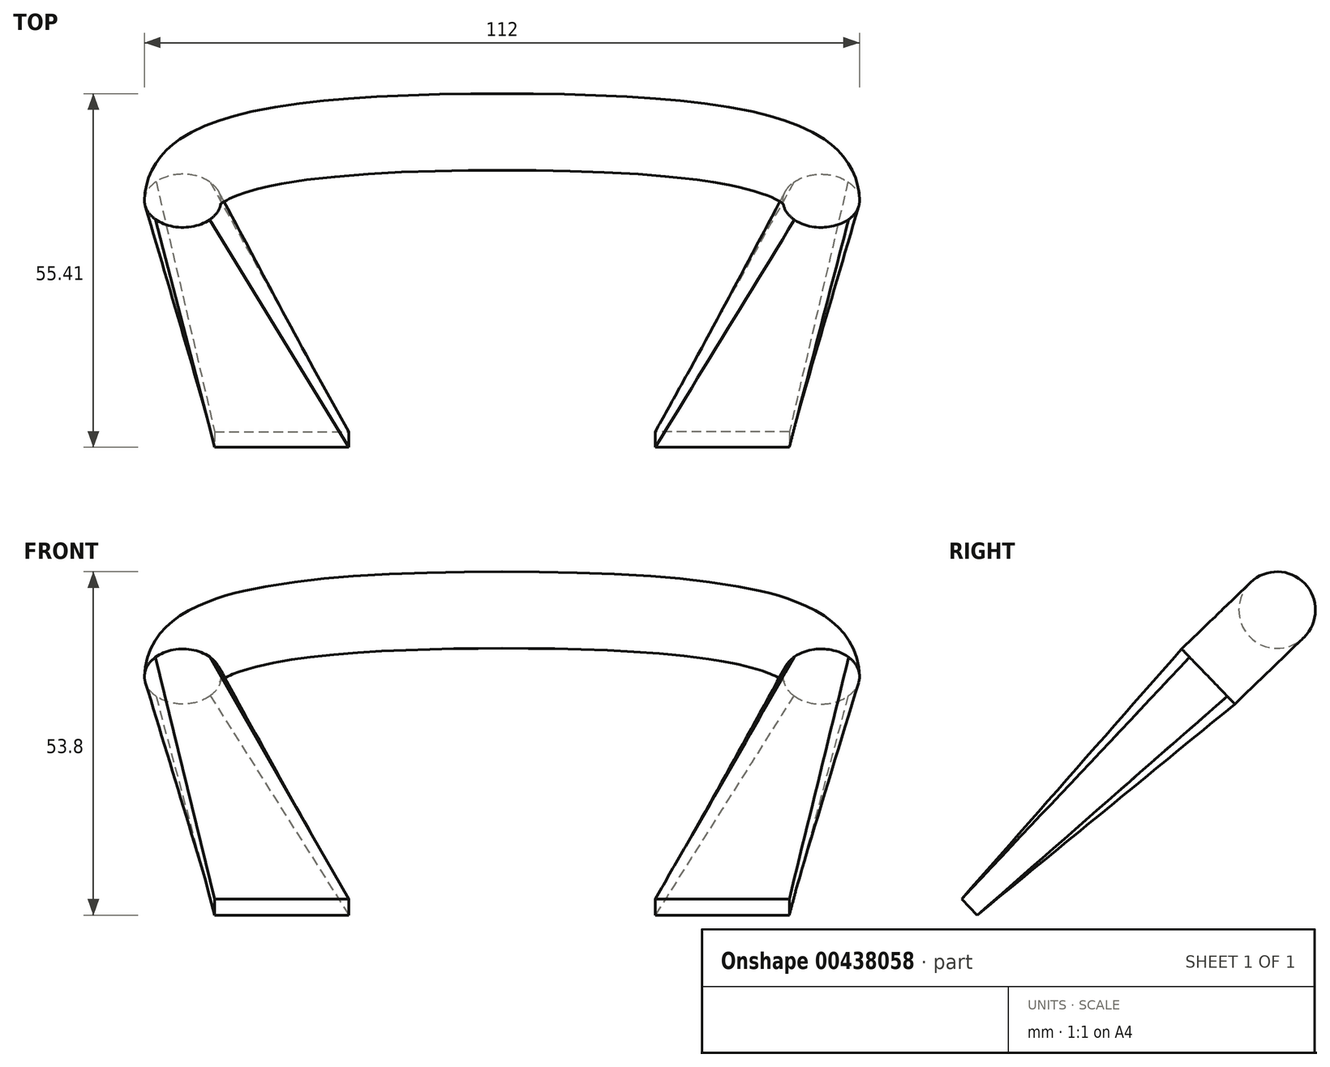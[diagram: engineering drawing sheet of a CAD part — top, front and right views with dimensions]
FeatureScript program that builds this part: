
annotation { "Feature Type Name" : "Feature", "Feature Type Description" : "" }
export const myFeature = defineFeature(function(context is Context, id is Id, definition is map)
    precondition{}
    {
        {
            var Q0;
            Q0=qCreatedBy(makeId("Top.planeOp"),FACE);
            var sketch = newSketch(context, id + "F0", { "sketchPlane" : qUnion([Q0])});
            skLineSegment(sketch, "E0", {"start": v(-34.5, 0) * mm, "end": v(34.5, 0) * mm, "construction": true});
            skLineSegment(sketch, "E1", {"start": v(0, 0) * mm, "end": v(0, 77.28) * mm, "construction": true});
            skPoint(sketch, "E2", {"position": v(-50, 52) * mm});
            skPoint(sketch, "E3", {"position": v(0, 67) * mm});
            skFitSpline(sketch, "E4", {"points": [v(0, 67) * mm, v(-50, 52) * mm], "startDerivative": vector(-102.6, 0) * mm, "endDerivative": vector(0, -30.42) * mm});
            skSolve(sketch);
        }
        {
            var Q0;
            Q0=qCreatedBy(makeId("Right.planeOp"),FACE);
            var sketch = newSketch(context, id + "F1", { "sketchPlane" : qUnion([Q0])});
            skPoint(sketch, "E5.0", {"position": v(67, 0) * mm});
            skCircle(sketch, "E6", {"center": v(67, 0) * mm, "radius": 6 * mm});
            skSolve(sketch);
        }
        {
            var Q0;
            Q0=makeQuery(id+"F1.imprint","IMPRINT",FACE,{"disambiguationData":[TD([[makeQuery(id+"F1.imprint","IMPRINT",EDGE,{"derivedFrom":sQuery(id+"F1.wireOp",EDGE,"E6")}),1.0]])]});
            var Q1;
            Q1=sQuery(id+"F0.wireOp",EDGE,"E4");
            sweep(context, id + "F2", {"profiles" : qUnion([Q0]), "path" : qUnion([Q1])});
        }
        {
            var Q0;
            Q0=qCreatedBy(makeId("Front.planeOp"),FACE);
            var sketch = newSketch(context, id + "F3", { "sketchPlane" : qUnion([Q0])});
            skLineSegment(sketch, "E7.0", {"start": v(-34.5, 0) * mm, "end": v(34.5, 0) * mm, "construction": true});
            skLineSegment(sketch, "E8.bottom", {"start": v(-45, -1.75) * mm, "end": v(-24, -1.75) * mm});
            skLineSegment(sketch, "E8.top", {"start": v(-45, 1.75) * mm, "end": v(-24, 1.75) * mm});
            skLineSegment(sketch, "E8.left", {"start": v(-45, -1.75) * mm, "end": v(-45, 1.75) * mm});
            skLineSegment(sketch, "E8.right", {"start": v(-24, -1.75) * mm, "end": v(-24, 1.75) * mm});
            skPoint(sketch, "E8.middle", {"position": v(-34.5, 0) * mm});
            skSolve(sketch);
        }
        {
            var Q0;
            Q0=makeQuery(id+"F2.opSweep","CAP_FACE",FACE,{"disambiguationData":[OSD([sQuery(id+"F0.wireOp",VERTEX,"E4.end"),sQuery(id+"F1.wireOp",EDGE,"E6")])],"isStart":false});
            var sketch = newSketch(context, id + "F4", { "sketchPlane" : qUnion([Q0])});
            skPoint(sketch, "E9.0", {"position": v(-50, 0) * mm});
            skPoint(sketch, "E10", {"position": v(-54.3, 4.19) * mm});
            skPoint(sketch, "E11", {"position": v(-45.7, 4.19) * mm});
            skPoint(sketch, "E12", {"position": v(-45.7, -4.19) * mm});
            skPoint(sketch, "E13", {"position": v(-54.3, -4.19) * mm});
            skSolve(sketch);
        }
        {
            var Q1;
            Q1=makeQuery(id+"F2.opSweep","CAP_FACE",FACE,{"disambiguationData":[OSD([sQuery(id+"F0.wireOp",VERTEX,"E4.end"),sQuery(id+"F1.wireOp",EDGE,"E6")])],"isStart":false});
            var Q2;
            Q2=makeQuery(id+"F3.imprint","IMPRINT",FACE,{"disambiguationData":[TD([[makeQuery(id+"F3.imprint","IMPRINT",EDGE,{"derivedFrom":sQuery(id+"F3.wireOp",EDGE,"E8.bottom")}),1.0]])]});
            var Q3;
            Q3=sQuery(id+"F3.wireOp",VERTEX,"E8.left.end");
            var Q4;
            Q4=sQuery(id+"F4.wireOp",VERTEX,"E10");
            loft(context, id + "F5", {"operationType" : NewBodyOperationType.ADD, "sheetProfilesArray" : [{ "sheetProfileEntities" : qUnion([Q1]) }, { "sheetProfileEntities" : qUnion([Q2]) }], "matchConnections" : true, "connections" : [{ "connectionEntities" : qUnion([Q3, Q4]), "connectionEdgeQueries" : qUnion([]), "connectionEdgeParameters" : [] }]});
        }
        {
            var Q0;
            Q0=makeQuery(id+"F2.opSweep","SWEPT_BODY",BODY,{"disambiguationData":[OSD([sQuery(id+"F0.wireOp",EDGE,"E4"),sQuery(id+"F1.wireOp",EDGE,"E6")])]});
            var Q1;
            Q1=qCreatedBy(makeId("Right.planeOp"),FACE);
            mirror(context, id + "F6", {"operationType" : NewBodyOperationType.ADD, "entities" : qUnion([Q0]), "mirrorPlane" : qUnion([Q1])});
        }
        {
            var Q0;
            Q0=qCreatedBy(makeId("Right.planeOp"),FACE);
            var sketch = newSketch(context, id + "F7", { "sketchPlane" : qUnion([Q0])});
            skFitSpline(sketch, "E14", {"points": [v(52, -6) * mm, v(49.83, -5.82) * mm, v(45.5, -5.47) * mm, v(39, -4.94) * mm, v(33.57, -4.5) * mm, v(29.24, -4.14) * mm, v(25.99, -3.87) * mm, v(22.74, -3.6) * mm, v(19.48, -3.34) * mm, v(16.23, -3.08) * mm, v(13.52, -2.86) * mm, v(11.36, -2.68) * mm, v(9.73, -2.55) * mm, v(8.1, -2.41) * mm, v(6.75, -2.3) * mm, v(5.67, -2.21) * mm, v(4.85, -2.15) * mm, v(4.04, -2.08) * mm, v(3.23, -2.01) * mm, v(2.55, -1.96) * mm, v(2, -1.91) * mm, v(1.6, -1.88) * mm, v(1.2, -1.85) * mm, v(0.86, -1.82) * mm, v(0.58, -1.8) * mm, v(0.42, -1.78) * mm, v(0.28, -1.77) * mm, v(0.2, -1.77) * mm, v(0.13, -1.76) * mm, v(0.07, -1.76) * mm, v(0.03, -1.75) * mm, v(0.01, -1.75) * mm, v(0, -1.75) * mm], "construction": true});
            skLineSegment(sketch, "E15", {"start": v(0, 0) * mm, "end": v(12, 10) * mm});
            skLineSegment(sketch, "E16", {"start": v(0, -1.75) * mm, "end": v(0, 0) * mm, "construction": true});
            skSolve(sketch);
        }
        {
            var Q0;
            Q0=makeQuery(id+"F2.opSweep","SWEPT_BODY",BODY,{"disambiguationData":[OSD([sQuery(id+"F0.wireOp",EDGE,"E4"),sQuery(id+"F1.wireOp",EDGE,"E6")])]});
            var Q1;
            Q1=sQuery(id+"F7.wireOp",EDGE,"E16");
            transform(context, id + "F8", {"entities" : qUnion([Q0]), "transformType" : TransformType.TRANSLATION_ENTITY, "oppositeDirectionEntity" : true, "transformLine" : qUnion([Q1]), "makeCopy" : false});
        }
        {
            var Q0;
            Q0=qCreatedBy(makeId("Right.planeOp"),FACE);
            var sketch = newSketch(context, id + "F9", { "sketchPlane" : qUnion([Q0])});
            skFitSpline(sketch, "E17", {"points": [v(0, 0) * mm, v(0, 0) * mm, v(0.02, 0) * mm, v(0.05, 0) * mm, v(0.1, 0) * mm, v(0.15, 0.01) * mm, v(0.2, 0.02) * mm, v(0.27, 0.02) * mm, v(0.4, 0.03) * mm, v(0.56, 0.05) * mm, v(0.83, 0.07) * mm, v(1.17, 0.1) * mm, v(1.58, 0.13) * mm, v(1.98, 0.16) * mm, v(2.53, 0.2) * mm, v(3.2, 0.26) * mm, v(4.02, 0.33) * mm, v(4.83, 0.4) * mm, v(5.64, 0.46) * mm, v(6.73, 0.55) * mm, v(8.08, 0.66) * mm, v(9.71, 0.8) * mm, v(11.34, 0.93) * mm, v(12.96, 1.06) * mm, v(14.59, 1.2) * mm, v(16.76, 1.37) * mm, v(19.47, 1.6) * mm, v(22.72, 1.86) * mm, v(25.98, 2.12) * mm, v(29.23, 2.39) * mm, v(33.57, 2.74) * mm, v(38.99, 3.19) * mm, v(45.5, 3.72) * mm, v(49.83, 4.07) * mm, v(52, 4.25) * mm], "construction": true});
            skLineSegment(sketch, "E18.0", {"start": v(0, 0) * mm, "end": v(12, 10) * mm});
            skLineSegment(sketch, "E19", {"start": v(0.01, 0) * mm, "end": v(21.35, 1.75) * mm});
            skSolve(sketch);
        }
        {
            var Q0;
            Q0=makeQuery(id+"F2.opSweep","SWEPT_BODY",BODY,{"disambiguationData":[OSD([sQuery(id+"F0.wireOp",EDGE,"E4"),sQuery(id+"F1.wireOp",EDGE,"E6")])]});
            var Q1;
            Q1=sQuery(id+"F0.wireOp",EDGE,"E0");
            transform(context, id + "F10", {"entities" : qUnion([Q0]), "transformType" : TransformType.ROTATION, "transformAxis" : qUnion([Q1]), "angle" : 44 * degree, "makeCopy" : false});
        }
    });
